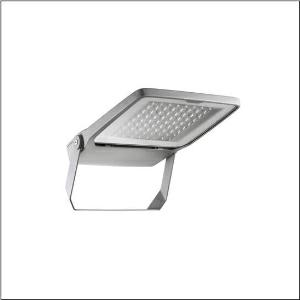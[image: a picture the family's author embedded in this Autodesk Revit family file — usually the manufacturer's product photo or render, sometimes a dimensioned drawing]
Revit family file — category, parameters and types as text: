
# Revit family: floodlight_fl_20_mini___rs17_5xa7671b2b1ac_3d4d
name_source: partatom
category: Lighting Fixtures
units: mm (PartAtom-declared; Revit-internal decimal feet)

## family parameters
Cut with Voids When Loaded = No
Host = Face
Light Source = No
Part Type = Normal
Room Calculation Point = No
Round Connector Dimension = Use Diameter
Shared = No

## types (1)
- Floodlight FL 20 mini  RS17 (1 x LED 4000K / CRI = 70 (unbekannt), 6810 lm, 4000K)
    Apparent Load = 51 VA
    CIE Flux Codes = 79 92 99 100 100
    Color Rendering = 70
    Color Temperature = 4000K
    Default Elevation = 1800 mm
    Description = Floodlight FL 20 mini, floodlight, primary light control with lens, of plastic, primary optical cover: protective disc, of toughened safety glass, transparent, light distribution: RS17, light emission: direct distribution, primary light characteristic: rotationally symmetric, installation type: surface-mounted, LED, High Power LED, rated luminous flux: 6.810lm, luminous efficacy: 134lm/W, light colour: 740, colour temperature: 4000K, control gear: ECG Basic, control: power reduction, overheat protection, electronic power reduction, with terminal, 5-pole, max. 2.5mm², mains connection: 220..240V, AC, 50/60Hz, rated input power: 51W, LED unit, of diecast aluminium, powder-coated, Siteco® metallic grey (DB 702S), corrosivity category C5 mid according to DIN EN ISO 12944, incl. 1x M20 cable gland for cable Ø 6.5..12mm, length: 446mm, width: 355mm, height: 62mm, housing frame, of diecast aluminium, powder-coated, Siteco® metallic grey (DB 702S), mounting bracket, of steel, powder-coated, Siteco® metallic grey (DB 702S), ON/OFF, protection rating (complete): IP66, insulation class (complete): insulation class I (protective earthing), certification: CE, ENEC, VDE, protection symbol: D, permissible operating ambient temperature: -40..+40°C, permissible operating ambient temperature for outdoor applications: -40..+50°C, standard: DIN EN 12944, packaging unit: 1 piece

Light Distribution: RS17
    Height = 62 mm  [stored 0.203412 ft]
    Lamp = 1 x LED 4000K / CRI >= 70 (unbekannt)
    Lamp Light Flux = 6810 lm
    Lamp count = 1
    Length = 467 mm
    Luminous efficacy = 134 lm/W
    Manufacturer = Siteco
    ModVariant = No
    Model = 5XA7671B2B1AC
    Mounting Place = Wall
    Mounting Type = Surface mounted
    Number of Poles = 1
    OnlyDefault = Yes
    Power Factor = 1
    Product Name = Floodlight FL 20 mini | RS17
    Product group = floodlight | wall mounted
    ProductGroupID = 2001
    Protection Class = Protection class I
    Protection Degree = IP 66
    RLX_Detail_Level = 1
    RLX_Emergency_Light_Flux = 0 lm
    RLX_Emergency_Type = 0
    RLX_Emergency_Type_DB = No
    RlxData = <blob elided: 65949 chars, md5=4bfe52e8>
    Socket = socket
    Standby Power = 0 W
    System Light Flux = 6810 lm
    System Power = 51 W
    Type Comments = Product without accessories
    Type Image = l_1005948.jpg
    URL = http://relux.com
    VarID = ---
    Voltage = 0 V
    Weight = 0.00 kg
    Width = 335 mm

note: [stored X ft] marks values corroborated as IEEE doubles in the binary element streams (Revit-internal decimal feet)

## geometry (parser evidence)
native form markers: Blend x4, Sweep x11
no freeform markers — native parametric forms only
